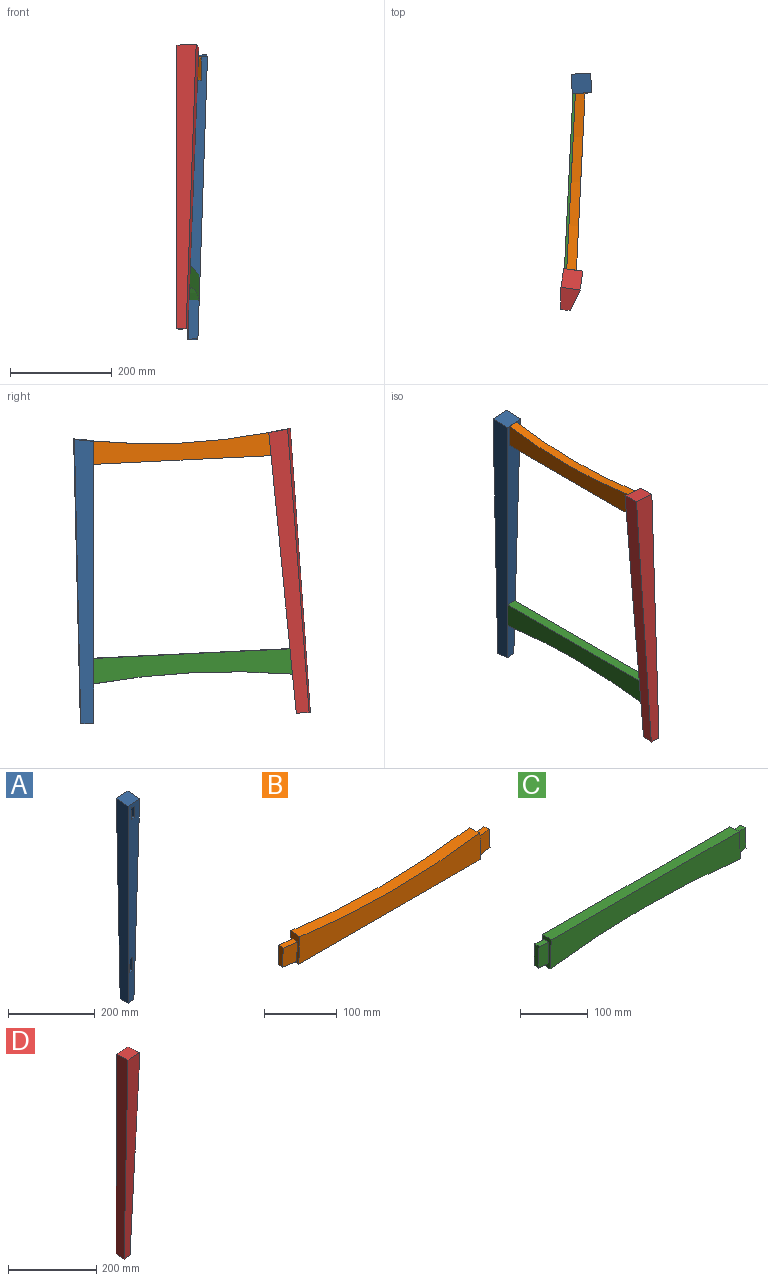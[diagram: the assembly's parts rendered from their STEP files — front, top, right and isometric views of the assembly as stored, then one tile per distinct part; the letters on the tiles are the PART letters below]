
ASSEMBLY  parts=4 mates=3
PART A: 16 faces, bbox 38.1x38.1x561.2 mm
  f0: plane 556.52x37.99mm, normal (0,-1,0), area 15185.6mm2, adj f2,f3,f4,f5,f6,f7,f8,f9
  f1: plane 561.18x38.1mm, normal (0,1,-0.02), area 16007.1mm2, adj f2,f3,f4,f5
  f2: plane 559.71x38.07mm, normal (-1,0,0), area 17681.2mm2, adj f0,f1,f4,f5
  f3: plane 560.68x38.1mm, normal (1,0,-0.03), area 17734.6mm2, adj f0,f1,f4,f5
  f4: plane 25.41x19.11mm, normal (0.03,-0.05,-1), area 485.8mm2, adj f0,f1,f2,f3
  f5: plane 38.1x38.1mm, normal (-0.04,-0.09,1), area 1455.4mm2, adj f0,f1,f2,f3
  f6: plane 26.99x9.53mm, normal (0,0,-1), area 257.1mm2, adj f0,f7,f9,f10
  f7: plane 31.75x26.99mm, normal (1,0,0), area 856.9mm2, adj f0,f6,f8,f10
  f8: plane 26.99x9.53mm, normal (0,0,1), area 257.1mm2, adj f0,f7,f9,f10
  f9: plane 31.75x26.99mm, normal (-1,0,0), area 856.9mm2, adj f0,f6,f8,f10
  f10: plane 31.75x9.53mm, normal (0,-1,0), area 302.4mm2, adj f6,f7,f8,f9
  f11: plane 20.64x9.53mm, normal (0,0,-1), area 196.6mm2, adj f0,f12,f14,f15
  f12: plane 38.1x20.64mm, normal (1,0,0), area 786.3mm2, adj f0,f11,f13,f15
  f13: plane 20.64x9.53mm, normal (0,0,1), area 196.6mm2, adj f0,f12,f14,f15
  f14: plane 38.1x20.64mm, normal (-1,0,0), area 786.3mm2, adj f0,f11,f13,f15
  f15: plane 38.1x9.53mm, normal (0,-1,0), area 362.9mm2, adj f11,f12,f13,f14
PART B: 16 faces, bbox 404x19.1x46 mm
  f0: plane 46.04x19.05mm, normal (-0.99,0.09,0.05), area 571.1mm2, adj f1,f2,f3,f4,f5,f6,f7,f15
  f1: plane 354.58x19.05mm, normal (0,-0.03,-1), area 6726.3mm2, adj f0,f2,f3,f9
  f2: plane 354.58x45.44mm, normal (0,-1,0), area 13043mm2, adj f0,f1,f9,f15
  f3: plane 351.24x45.79mm, normal (0,1,0), area 13099.2mm2, adj f0,f1,f9,f15
  f4: plane 26.11x11.74mm, normal (0.05,0,1), area 241.9mm2, adj f0,f5,f7,f8
  f5: plane 32.95x26.83mm, normal (0.09,1,0), area 806.5mm2, adj f0,f4,f6,f8
  f6: plane 26.11x11.74mm, normal (-0.05,0,-1), area 241.9mm2, adj f0,f5,f7,f8
  f7: plane 32.95x26.83mm, normal (-0.09,-1,0), area 806.4mm2, adj f0,f4,f6,f8
  f8: plane 31.75x9.49mm, normal (-0.99,0.09,0.05), area 302.4mm2, adj f4,f5,f6,f7
  f9: plane 46.04x19.05mm, normal (0.99,0.09,0.05), area 571.1mm2, adj f1,f2,f3,f10,f11,f12,f13,f15
  f10: plane 26.11x11.74mm, normal (-0.05,0,1), area 241.9mm2, adj f9,f11,f13,f14
  f11: plane 32.95x26.83mm, normal (-0.09,1,0), area 806.5mm2, adj f9,f10,f12,f14
  f12: plane 26.11x11.74mm, normal (0.05,0,-1), area 241.9mm2, adj f9,f11,f13,f14
  f13: plane 32.95x26.83mm, normal (0.09,-1,0), area 806.4mm2, adj f9,f10,f12,f14
  f14: plane 31.75x9.49mm, normal (0.99,0.09,0.05), area 302.4mm2, adj f10,f11,f12,f13
  f15: cylinder r=1212.89mm len=350.12mm, axis (0,-1,0), area 6660.7mm2, adj f0,f2,f3,f9
PART C: 16 faces, bbox 432.6x19.1x50.8 mm
  f0: plane 391.17x19.05mm, normal (0,0.03,1), area 7423.6mm2, adj f1,f2,f3,f9
  f1: plane 50.8x19.05mm, normal (-0.99,0.09,0.05), area 602mm2, adj f0,f2,f3,f4,f5,f6,f7,f15
  f2: plane 396.16x50.8mm, normal (0,-1,0), area 16641.2mm2, adj f0,f1,f9,f15
  f3: plane 392.74x49.98mm, normal (0,1,0), area 16236.7mm2, adj f0,f1,f9,f15
  f4: plane 38.98x20.82mm, normal (0.09,1,0), area 725.8mm2, adj f1,f5,f7,f8
  f5: plane 19.8x11.18mm, normal (-0.05,0,-1), area 181.5mm2, adj f1,f4,f6,f8
  f6: plane 38.98x20.82mm, normal (-0.09,-1,0), area 725.8mm2, adj f1,f5,f7,f8
  f7: plane 19.8x11.18mm, normal (0.05,0,1), area 181.5mm2, adj f1,f4,f6,f8
  f8: plane 38.1x9.49mm, normal (-0.99,0.09,0.05), area 362.9mm2, adj f4,f5,f6,f7
  f9: plane 50.8x19.05mm, normal (0.99,0.09,0.05), area 602mm2, adj f0,f2,f3,f10,f11,f12,f13,f15
  f10: plane 38.98x20.82mm, normal (-0.09,1,0), area 725.8mm2, adj f9,f11,f13,f14
  f11: plane 19.8x11.18mm, normal (0.05,0,-1), area 181.5mm2, adj f9,f10,f12,f14
  f12: plane 38.98x20.82mm, normal (0.09,-1,0), area 725.8mm2, adj f9,f11,f13,f14
  f13: plane 19.8x11.18mm, normal (-0.05,0,1), area 181.5mm2, adj f9,f10,f12,f14
  f14: plane 38.1x9.49mm, normal (0.99,0.09,0.05), area 362.9mm2, adj f10,f11,f12,f13
  f15: cylinder r=1551.04mm len=396.16mm, axis (0,-1,0), area 7534.6mm2, adj f1,f2,f3,f9
PART D: 16 faces, bbox 38.1x38.1x561.2 mm
  f0: plane 556.52x37.99mm, normal (0,1,0), area 15185.6mm2, adj f2,f3,f4,f5,f6,f7,f8,f9
  f1: plane 561.18x38.1mm, normal (0,-1,-0.02), area 16007.1mm2, adj f2,f3,f4,f5
  f2: plane 559.71x38.07mm, normal (-1,0,0), area 17681.2mm2, adj f0,f1,f4,f5
  f3: plane 560.68x38.1mm, normal (1,0,-0.03), area 17734.6mm2, adj f0,f1,f4,f5
  f4: plane 25.41x19.11mm, normal (0.03,0.05,-1), area 485.8mm2, adj f0,f1,f2,f3
  f5: plane 38.1x38.1mm, normal (-0.04,0.09,1), area 1455.4mm2, adj f0,f1,f2,f3
  f6: plane 26.99x9.53mm, normal (0,0,-1), area 257.1mm2, adj f0,f7,f9,f10
  f7: plane 31.75x26.99mm, normal (1,0,0), area 856.9mm2, adj f0,f6,f8,f10
  f8: plane 26.99x9.53mm, normal (0,0,1), area 257.1mm2, adj f0,f7,f9,f10
  f9: plane 31.75x26.99mm, normal (-1,0,0), area 856.9mm2, adj f0,f6,f8,f10
  f10: plane 31.75x9.53mm, normal (0,1,0), area 302.4mm2, adj f6,f7,f8,f9
  f11: plane 20.64x9.53mm, normal (0,0,-1), area 196.6mm2, adj f0,f12,f14,f15
  f12: plane 38.1x20.64mm, normal (1,0,0), area 786.3mm2, adj f0,f11,f13,f15
  f13: plane 20.64x9.53mm, normal (0,0,1), area 196.6mm2, adj f0,f12,f14,f15
  f14: plane 38.1x20.64mm, normal (-1,0,0), area 786.3mm2, adj f0,f11,f13,f15
  f15: plane 38.1x9.53mm, normal (0,1,0), area 362.9mm2, adj f11,f12,f13,f14
PLACE A rot(axis=(0,0,1),2.3deg) t=(129.61,238.19,460.25)mm
PLACE B rot(axis=(-0.02,0.03,1),87.2deg) t=(109.04,43.52,418.59)mm
PLACE C rot(axis=(-0.02,0.03,1),87.2deg) t=(103.27,22.64,-12.93)mm
PLACE D rot(axis=(-0.58,-0.01,-0.81),9.7deg) t=(110.76,-147.3,479.13)mm
MATE fastened C.f9 <-> A.f0  axis (0.04,-1,0) through (122.45,218.93,2.79)mm
MATE fastened D.f0 <-> C.f1  axis (0.14,0.99,-0.1) through (103.32,-172.11,21.94)mm
MATE fastened B.f0 <-> D.f0  axis (0.14,0.99,-0.1) through (110.08,-131.14,446.18)mm
